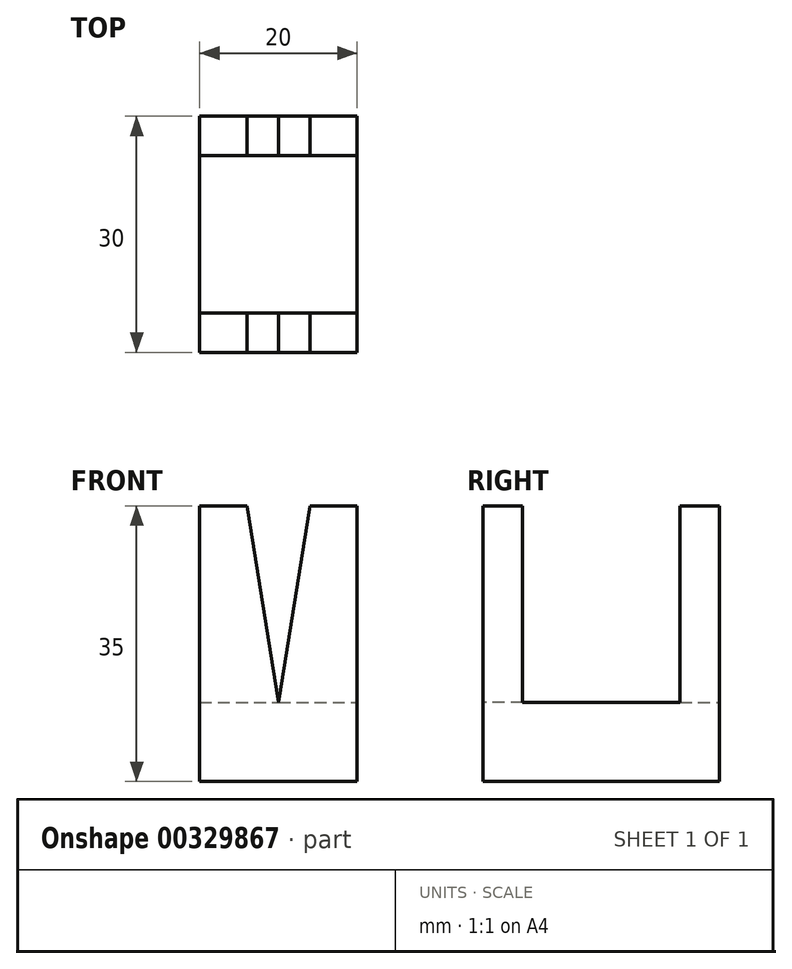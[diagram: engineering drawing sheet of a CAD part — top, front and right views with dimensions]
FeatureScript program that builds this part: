
annotation { "Feature Type Name" : "Feature", "Feature Type Description" : "" }
export const myFeature = defineFeature(function(context is Context, id is Id, definition is map)
    precondition{}
    {
        {
            var Q0;
            Q0=qCreatedBy(makeId("Front.planeOp"),FACE);
            var sketch = newSketch(context, id + "F0", { "sketchPlane" : qUnion([Q0])});
            skLineSegment(sketch, "E0", {"start": v(0, 0) * mm, "end": v(0, 35) * mm});
            skLineSegment(sketch, "E1", {"start": v(0, 35) * mm, "end": v(6, 35) * mm});
            skLineSegment(sketch, "E2", {"start": v(6, 35) * mm, "end": v(10, 10) * mm});
            skLineSegment(sketch, "E3", {"start": v(10, 10) * mm, "end": v(10, 0) * mm, "construction": true});
            skLineSegment(sketch, "E4", {"start": v(10, 0) * mm, "end": v(0, 0) * mm});
            skLineSegment(sketch, "E5.MirrorCS", {"start": v(14, 35) * mm, "end": v(10, 10) * mm});
            skLineSegment(sketch, "E6.MirrorCS", {"start": v(20, 35) * mm, "end": v(14, 35) * mm});
            skLineSegment(sketch, "E7.MirrorCS", {"start": v(20, 0) * mm, "end": v(20, 35) * mm});
            skLineSegment(sketch, "E8.MirrorCS", {"start": v(10, 0) * mm, "end": v(20, 0) * mm});
            skSolve(sketch);
        }
        {
            var Q0;
            Q0=makeQuery(id+"F0.imprint","IMPRINT",FACE,{"disambiguationData":[TD([[makeQuery(id+"F0.imprint","IMPRINT",EDGE,{"derivedFrom":sQuery(id+"F0.wireOp",EDGE,"E0")}),-1.0]])]});
            extrude(context, id + "F1", {"entities" : qUnion([Q0]), "depth" : 5 * mm, "offsetDistance" : 25 * mm});
        }
        {
            var Q0;
            Q0=makeQuery(id+"F1.opExtrude","CAP_FACE",FACE,{"disambiguationData":[OSD([sQuery(id+"F0.wireOp",EDGE,"E0"),sQuery(id+"F0.wireOp",EDGE,"E1"),sQuery(id+"F0.wireOp",EDGE,"E2"),sQuery(id+"F0.wireOp",EDGE,"E4"),sQuery(id+"F0.wireOp",EDGE,"E5.MirrorCS"),sQuery(id+"F0.wireOp",EDGE,"E6.MirrorCS"),sQuery(id+"F0.wireOp",EDGE,"E7.MirrorCS"),sQuery(id+"F0.wireOp",EDGE,"E8.MirrorCS")])],"isStart":false});
            var sketch = newSketch(context, id + "F2", { "sketchPlane" : qUnion([Q0])});
            skLineSegment(sketch, "E9.bottom", {"start": v(0, 0) * mm, "end": v(20, 0) * mm});
            skLineSegment(sketch, "E9.top", {"start": v(0, 10) * mm, "end": v(20, 10) * mm});
            skLineSegment(sketch, "E9.left", {"start": v(0, 0) * mm, "end": v(0, 10) * mm});
            skLineSegment(sketch, "E9.right", {"start": v(20, 0) * mm, "end": v(20, 10) * mm});
            skSolve(sketch);
        }
        {
            var Q0;
            Q0 = qSketchRegion(id + "F2", true);
            extrude(context, id + "F3", {"entities" : qUnion([Q0]), "operationType" : NewBodyOperationType.ADD, "depth" : 10 * mm, "offsetDistance" : 25 * mm});
        }
        {
            var Q0;
            Q0=makeQuery(id+"F1.opExtrude","SWEPT_BODY",BODY,{"disambiguationData":[OSD([sQuery(id+"F0.wireOp",EDGE,"E0"),sQuery(id+"F0.wireOp",EDGE,"E1"),sQuery(id+"F0.wireOp",EDGE,"E2"),sQuery(id+"F0.wireOp",EDGE,"E4"),sQuery(id+"F0.wireOp",EDGE,"E5.MirrorCS"),sQuery(id+"F0.wireOp",EDGE,"E6.MirrorCS"),sQuery(id+"F0.wireOp",EDGE,"E7.MirrorCS"),sQuery(id+"F0.wireOp",EDGE,"E8.MirrorCS")])]});
            var Q1;
            Q1=makeQuery(id+"F3.opExtrude","CAP_FACE",FACE,{"disambiguationData":[OSD([sQuery(id+"F2.wireOp",EDGE,"E9.bottom"),sQuery(id+"F2.wireOp",EDGE,"E9.top"),sQuery(id+"F2.wireOp",EDGE,"E9.left"),sQuery(id+"F2.wireOp",EDGE,"E9.right")])],"isStart":false});
            mirror(context, id + "F4", {"operationType" : NewBodyOperationType.ADD, "entities" : qUnion([Q0]), "mirrorPlane" : qUnion([Q1])});
        }
    });
